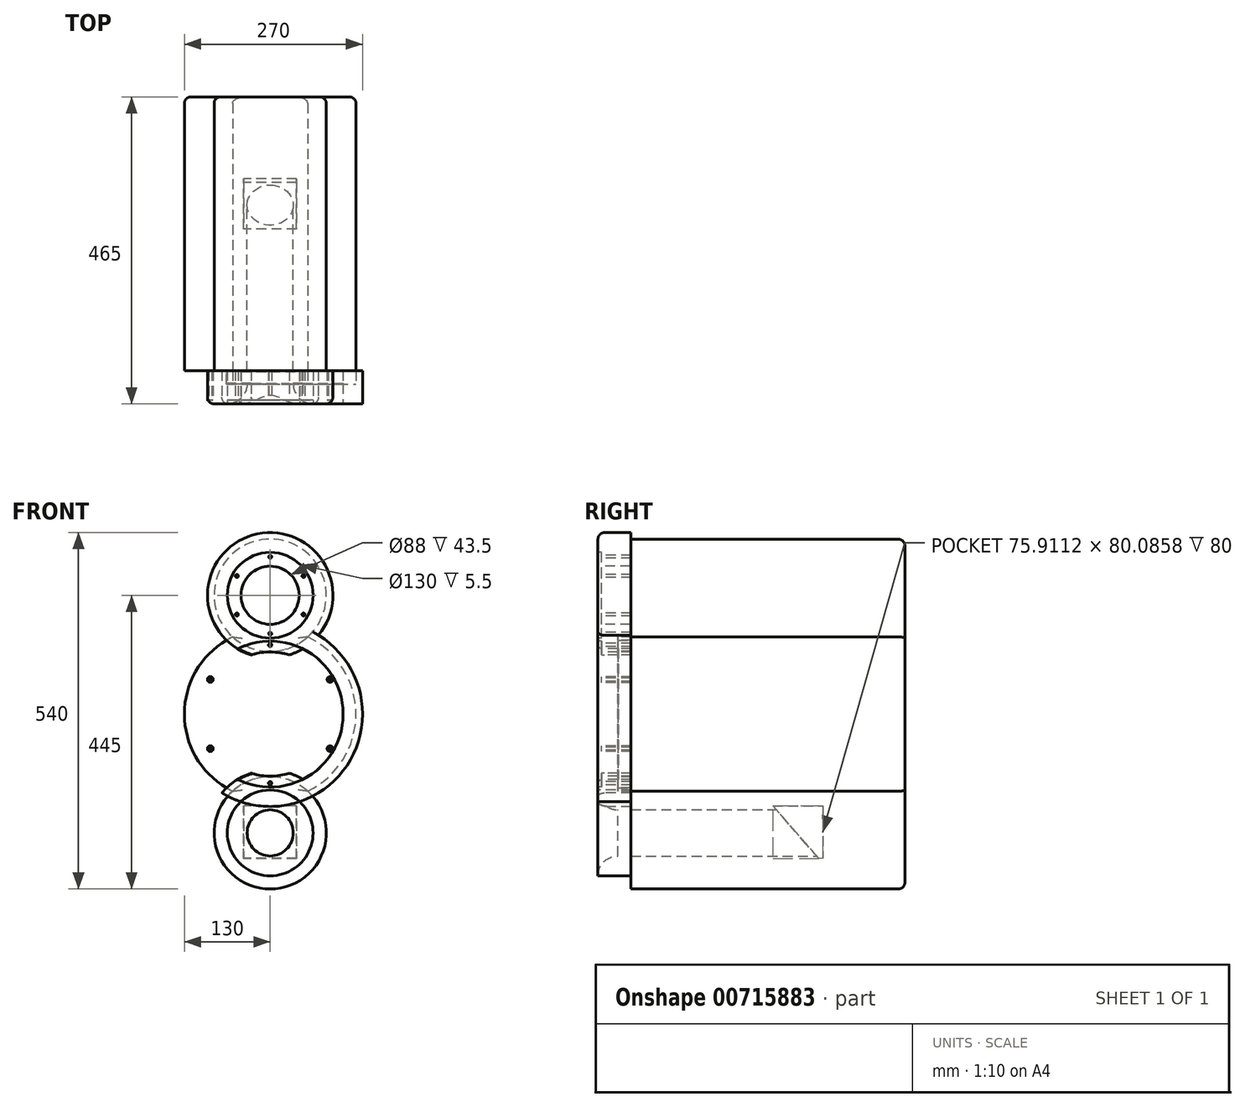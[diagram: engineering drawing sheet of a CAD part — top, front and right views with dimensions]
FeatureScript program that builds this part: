
annotation { "Feature Type Name" : "Feature", "Feature Type Description" : "" }
export const myFeature = defineFeature(function(context is Context, id is Id, definition is map)
    precondition{}
    {
        {
            var Q0;
            Q0=qCreatedBy(makeId("Front.planeOp"),FACE);
            var sketch = newSketch(context, id + "F0", { "sketchPlane" : qUnion([Q0])});
            skCircle(sketch, "E0", {"center": v(0, 0) * mm, "radius": 94 * mm});
            skCircle(sketch, "E1", {"center": v(0, 0) * mm, "radius": 110.5 * mm});
            skCircle(sketch, "E2", {"center": v(0, 180) * mm, "radius": 65 * mm});
            skCircle(sketch, "E3", {"center": v(0, 180) * mm, "radius": 44 * mm});
            skCircle(sketch, "E4", {"center": v(0, 104.75) * mm, "radius": 2.5 * mm});
            skCircle(sketch, "E5", {"center": v(0, 104.75) * mm, "radius": 4.4 * mm});
            skCircle(sketch, "E6.1.0", {"center": v(-90.72, 52.38) * mm, "radius": 4.4 * mm});
            skCircle(sketch, "E6.1.1", {"center": v(-90.72, 52.38) * mm, "radius": 2.5 * mm});
            skCircle(sketch, "E6.2.0", {"center": v(-90.72, -52.37) * mm, "radius": 4.4 * mm});
            skCircle(sketch, "E6.2.1", {"center": v(-90.72, -52.37) * mm, "radius": 2.5 * mm});
            skCircle(sketch, "E6.3.0", {"center": v(0, -104.75) * mm, "radius": 4.4 * mm});
            skCircle(sketch, "E6.3.1", {"center": v(0, -104.75) * mm, "radius": 2.5 * mm});
            skCircle(sketch, "E6.4.0", {"center": v(90.72, -52.38) * mm, "radius": 4.4 * mm});
            skCircle(sketch, "E6.4.1", {"center": v(90.72, -52.38) * mm, "radius": 2.5 * mm});
            skCircle(sketch, "E6.5.0", {"center": v(90.72, 52.38) * mm, "radius": 4.4 * mm});
            skCircle(sketch, "E6.5.1", {"center": v(90.72, 52.38) * mm, "radius": 2.5 * mm});
            skCircle(sketch, "E7", {"center": v(0, 238.25) * mm, "radius": 2.25 * mm});
            skCircle(sketch, "E8", {"center": v(0, 238.25) * mm, "radius": 4.25 * mm});
            skCircle(sketch, "E9.1.0", {"center": v(-50.45, 209.12) * mm, "radius": 4.25 * mm});
            skCircle(sketch, "E9.1.1", {"center": v(-50.45, 209.12) * mm, "radius": 2.25 * mm});
            skCircle(sketch, "E9.2.0", {"center": v(-50.45, 150.88) * mm, "radius": 4.25 * mm});
            skCircle(sketch, "E9.2.1", {"center": v(-50.45, 150.88) * mm, "radius": 2.25 * mm});
            skCircle(sketch, "E9.3.0", {"center": v(0, 121.75) * mm, "radius": 4.25 * mm});
            skCircle(sketch, "E9.3.1", {"center": v(0, 121.75) * mm, "radius": 2.25 * mm});
            skCircle(sketch, "E9.4.0", {"center": v(50.45, 150.87) * mm, "radius": 4.25 * mm});
            skCircle(sketch, "E9.4.1", {"center": v(50.45, 150.87) * mm, "radius": 2.25 * mm});
            skCircle(sketch, "E9.5.0", {"center": v(50.45, 209.12) * mm, "radius": 4.25 * mm});
            skCircle(sketch, "E9.5.1", {"center": v(50.45, 209.12) * mm, "radius": 2.25 * mm});
            skCircle(sketch, "E10", {"center": v(0, 180) * mm, "radius": 95 * mm});
            skCircle(sketch, "E11", {"center": v(0, 0) * mm, "radius": 140 * mm});
            skCircle(sketch, "E12", {"center": v(0, -180) * mm, "radius": 35 * mm});
            skCircle(sketch, "E13", {"center": v(0, -180) * mm, "radius": 95 * mm});
            skCircle(sketch, "E14", {"center": v(0, -180) * mm, "radius": 65 * mm});
            skSolve(sketch);
        }
        {
            var Q0;
            {var subQ0=sQuery(id+"F0.wireOp",EDGE,"E13");var subQ1=sQuery(id+"F0.wireOp",EDGE,"E11");var subQ2=makeQuery(id+"F0.imprint","INTERSECT",VERTEX,{"disambiguationData":[OD(0.0)],"derivedFrom":[subQ1,subQ0]});Q0=makeQuery(id+"F0.imprint","IMPRINT",FACE,{"disambiguationData":[TD([[makeQuery(id+"F0.imprint","IMPRINT",EDGE,{"disambiguationData":[TD([[subQ2,-1.0]])],"derivedFrom":subQ1}),-1.0]])]});}
            var Q1;
            Q1=makeQuery(id+"F0.imprint","IMPRINT",FACE,{"disambiguationData":[TD([[makeQuery(id+"F0.imprint","IMPRINT",EDGE,{"derivedFrom":sQuery(id+"F0.wireOp",EDGE,"E12")}),-1.0]])]});
            var Q2;
            Q2=makeQuery(id+"F0.imprint","IMPRINT",FACE,{"disambiguationData":[TD([[makeQuery(id+"F0.imprint","IMPRINT",EDGE,{"derivedFrom":sQuery(id+"F0.wireOp",EDGE,"E6.3.0")}),-1.0]])]});
            var Q3;
            {var subQ6=sQuery(id+"F0.wireOp",EDGE,"E10");var subQ8=sQuery(id+"F0.wireOp",EDGE,"E0");var subQ9=makeQuery(id+"F0.imprint","INTERSECT",VERTEX,{"disambiguationData":[OD(1.0)],"derivedFrom":[subQ8,subQ6]});Q3=makeQuery(id+"F0.imprint","IMPRINT",FACE,{"disambiguationData":[TD([[makeQuery(id+"F0.imprint","IMPRINT",EDGE,{"disambiguationData":[TD([[subQ9,1.0]])],"derivedFrom":subQ8}),-1.0]])]});}
            var Q4;
            {var subQ0=sQuery(id+"F0.wireOp",EDGE,"E10");var subQ1=sQuery(id+"F0.wireOp",EDGE,"E1");var subQ2=makeQuery(id+"F0.imprint","INTERSECT",VERTEX,{"disambiguationData":[OD(1.0)],"derivedFrom":[subQ1,subQ0]});Q4=makeQuery(id+"F0.imprint","IMPRINT",FACE,{"disambiguationData":[TD([[makeQuery(id+"F0.imprint","IMPRINT",EDGE,{"disambiguationData":[TD([[subQ2,1.0]])],"derivedFrom":subQ1}),-1.0]])]});}
            var Q5;
            {var subQ0=sQuery(id+"F0.wireOp",EDGE,"E10");var subQ1=sQuery(id+"F0.wireOp",EDGE,"E1");var subQ2=makeQuery(id+"F0.imprint","INTERSECT",VERTEX,{"disambiguationData":[OD(0.0)],"derivedFrom":[subQ1,subQ0]});Q5=makeQuery(id+"F0.imprint","IMPRINT",FACE,{"disambiguationData":[TD([[makeQuery(id+"F0.imprint","IMPRINT",EDGE,{"disambiguationData":[TD([[subQ2,-1.0]])],"derivedFrom":subQ1}),-1.0]])]});}
            var Q6;
            {var subQ4=sQuery(id+"F0.wireOp",EDGE,"E0");var subQ6=sQuery(id+"F0.wireOp",EDGE,"E10");var subQ10=makeQuery(id+"F0.imprint","INTERSECT",VERTEX,{"disambiguationData":[OD(0.0)],"derivedFrom":[subQ4,subQ6]});Q6=makeQuery(id+"F0.imprint","IMPRINT",FACE,{"disambiguationData":[TD([[makeQuery(id+"F0.imprint","IMPRINT",EDGE,{"disambiguationData":[TD([[subQ10,-1.0]])],"derivedFrom":subQ4}),-1.0]])]});}
            var Q7;
            {var subQ1=sQuery(id+"F0.wireOp",EDGE,"E10");var subQ3=sQuery(id+"F0.wireOp",EDGE,"E1");var subQ4=makeQuery(id+"F0.imprint","INTERSECT",VERTEX,{"disambiguationData":[OD(0.0)],"derivedFrom":[subQ3,subQ1]});Q7=makeQuery(id+"F0.imprint","IMPRINT",FACE,{"disambiguationData":[TD([[makeQuery(id+"F0.imprint","IMPRINT",EDGE,{"disambiguationData":[TD([[subQ4,1.0]])],"derivedFrom":subQ3}),-1.0]])]});}
            var Q8;
            Q8=makeQuery(id+"F0.imprint","IMPRINT",FACE,{"disambiguationData":[TD([[makeQuery(id+"F0.imprint","IMPRINT",EDGE,{"derivedFrom":sQuery(id+"F0.wireOp",EDGE,"E5")}),-1.0]])]});
            var Q9;
            Q9=makeQuery(id+"F0.imprint","IMPRINT",FACE,{"disambiguationData":[TD([[makeQuery(id+"F0.imprint","IMPRINT",EDGE,{"derivedFrom":sQuery(id+"F0.wireOp",EDGE,"E9.2.0")}),-1.0]])]});
            var Q10;
            Q10=makeQuery(id+"F0.imprint","IMPRINT",FACE,{"disambiguationData":[TD([[makeQuery(id+"F0.imprint","IMPRINT",EDGE,{"derivedFrom":sQuery(id+"F0.wireOp",EDGE,"E8")}),-1.0]])]});
            var Q11;
            {var subQ0=sQuery(id+"F0.wireOp",EDGE,"E11");var subQ1=sQuery(id+"F0.wireOp",EDGE,"E2");var subQ2=makeQuery(id+"F0.imprint","INTERSECT",VERTEX,{"disambiguationData":[OD(0.0)],"derivedFrom":[subQ1,subQ0]});Q11=makeQuery(id+"F0.imprint","IMPRINT",FACE,{"disambiguationData":[TD([[makeQuery(id+"F0.imprint","IMPRINT",EDGE,{"disambiguationData":[TD([[subQ2,-1.0]])],"derivedFrom":subQ1}),-1.0]])]});}
            var Q12;
            Q12=makeQuery(id+"F0.imprint","IMPRINT",FACE,{"disambiguationData":[TD([[makeQuery(id+"F0.imprint","IMPRINT",EDGE,{"derivedFrom":sQuery(id+"F0.wireOp",EDGE,"E6.3.0")}),1.0]])]});
            var Q13;
            {var subQ0=sQuery(id+"F0.wireOp",EDGE,"E13");var subQ1=sQuery(id+"F0.wireOp",EDGE,"E6.2.0");var subQ2=makeQuery(id+"F0.imprint","INTERSECT",VERTEX,{"disambiguationData":[OD(0.0)],"derivedFrom":[subQ1,subQ0]});Q13=makeQuery(id+"F0.imprint","IMPRINT",FACE,{"disambiguationData":[TD([[makeQuery(id+"F0.imprint","IMPRINT",EDGE,{"disambiguationData":[TD([[subQ2,1.0]])],"derivedFrom":subQ1}),1.0]])]});}
            var Q14;
            {var subQ0=sQuery(id+"F0.wireOp",EDGE,"E13");var subQ1=sQuery(id+"F0.wireOp",EDGE,"E6.2.0");var subQ2=makeQuery(id+"F0.imprint","INTERSECT",VERTEX,{"disambiguationData":[OD(0.0)],"derivedFrom":[subQ1,subQ0]});Q14=makeQuery(id+"F0.imprint","IMPRINT",FACE,{"disambiguationData":[TD([[makeQuery(id+"F0.imprint","IMPRINT",EDGE,{"disambiguationData":[TD([[subQ2,-1.0]])],"derivedFrom":subQ1}),1.0]])]});}
            var Q15;
            Q15=makeQuery(id+"F0.imprint","IMPRINT",FACE,{"disambiguationData":[TD([[makeQuery(id+"F0.imprint","IMPRINT",EDGE,{"derivedFrom":sQuery(id+"F0.wireOp",EDGE,"E6.1.0")}),1.0]])]});
            var Q16;
            Q16=makeQuery(id+"F0.imprint","IMPRINT",FACE,{"disambiguationData":[TD([[makeQuery(id+"F0.imprint","IMPRINT",EDGE,{"derivedFrom":sQuery(id+"F0.wireOp",EDGE,"E4")}),-1.0]])]});
            var Q17;
            Q17=makeQuery(id+"F0.imprint","IMPRINT",FACE,{"disambiguationData":[TD([[makeQuery(id+"F0.imprint","IMPRINT",EDGE,{"derivedFrom":sQuery(id+"F0.wireOp",EDGE,"E9.3.0")}),1.0]])]});
            var Q18;
            Q18=makeQuery(id+"F0.imprint","IMPRINT",FACE,{"disambiguationData":[TD([[makeQuery(id+"F0.imprint","IMPRINT",EDGE,{"derivedFrom":sQuery(id+"F0.wireOp",EDGE,"E6.5.0")}),1.0]])]});
            var Q19;
            {var subQ0=sQuery(id+"F0.wireOp",EDGE,"E13");var subQ1=sQuery(id+"F0.wireOp",EDGE,"E6.4.0");var subQ2=makeQuery(id+"F0.imprint","INTERSECT",VERTEX,{"disambiguationData":[OD(0.0)],"derivedFrom":[subQ1,subQ0]});Q19=makeQuery(id+"F0.imprint","IMPRINT",FACE,{"disambiguationData":[TD([[makeQuery(id+"F0.imprint","IMPRINT",EDGE,{"disambiguationData":[TD([[subQ2,-1.0]])],"derivedFrom":subQ1}),1.0]])]});}
            var Q20;
            {var subQ0=sQuery(id+"F0.wireOp",EDGE,"E13");var subQ1=sQuery(id+"F0.wireOp",EDGE,"E6.4.0");var subQ2=makeQuery(id+"F0.imprint","INTERSECT",VERTEX,{"disambiguationData":[OD(0.0)],"derivedFrom":[subQ1,subQ0]});Q20=makeQuery(id+"F0.imprint","IMPRINT",FACE,{"disambiguationData":[TD([[makeQuery(id+"F0.imprint","IMPRINT",EDGE,{"disambiguationData":[TD([[subQ2,1.0]])],"derivedFrom":subQ1}),1.0]])]});}
            var Q21;
            Q21=makeQuery(id+"F0.imprint","IMPRINT",FACE,{"disambiguationData":[TD([[makeQuery(id+"F0.imprint","IMPRINT",EDGE,{"derivedFrom":sQuery(id+"F0.wireOp",EDGE,"E9.4.0")}),1.0]])]});
            var Q22;
            Q22=makeQuery(id+"F0.imprint","IMPRINT",FACE,{"disambiguationData":[TD([[makeQuery(id+"F0.imprint","IMPRINT",EDGE,{"derivedFrom":sQuery(id+"F0.wireOp",EDGE,"E9.2.0")}),1.0]])]});
            var Q23;
            Q23=makeQuery(id+"F0.imprint","IMPRINT",FACE,{"disambiguationData":[TD([[makeQuery(id+"F0.imprint","IMPRINT",EDGE,{"derivedFrom":sQuery(id+"F0.wireOp",EDGE,"E9.1.0")}),1.0]])]});
            var Q24;
            Q24=makeQuery(id+"F0.imprint","IMPRINT",FACE,{"disambiguationData":[TD([[makeQuery(id+"F0.imprint","IMPRINT",EDGE,{"derivedFrom":sQuery(id+"F0.wireOp",EDGE,"E7")}),-1.0]])]});
            var Q25;
            Q25=makeQuery(id+"F0.imprint","IMPRINT",FACE,{"disambiguationData":[TD([[makeQuery(id+"F0.imprint","IMPRINT",EDGE,{"derivedFrom":sQuery(id+"F0.wireOp",EDGE,"E9.5.0")}),1.0]])]});
            var Q26;
            {var subQ0=sQuery(id+"F0.wireOp",EDGE,"E13");var subQ7=sQuery(id+"F0.wireOp",EDGE,"E1");var subQ9=makeQuery(id+"F0.imprint","INTERSECT",VERTEX,{"disambiguationData":[OD(0.0)],"derivedFrom":[subQ7,subQ0]});Q26=makeQuery(id+"F0.imprint","IMPRINT",FACE,{"disambiguationData":[TD([[makeQuery(id+"F0.imprint","IMPRINT",EDGE,{"disambiguationData":[TD([[subQ9,-1.0]])],"derivedFrom":subQ7}),-1.0]])]});}
            var Q27;
            Q27=makeQuery(id+"F0.imprint","IMPRINT",FACE,{"disambiguationData":[TD([[makeQuery(id+"F0.imprint","IMPRINT",EDGE,{"derivedFrom":sQuery(id+"F0.wireOp",EDGE,"E6.4.0")}),1.0]])]});
            var Q28;
            Q28=makeQuery(id+"F0.imprint","IMPRINT",FACE,{"disambiguationData":[TD([[makeQuery(id+"F0.imprint","IMPRINT",EDGE,{"derivedFrom":sQuery(id+"F0.wireOp",EDGE,"E6.2.0")}),1.0]])]});
            var Q29;
            Q29=makeQuery(id+"F0.imprint","IMPRINT",FACE,{"disambiguationData":[TD([[makeQuery(id+"F0.imprint","IMPRINT",EDGE,{"derivedFrom":sQuery(id+"F0.wireOp",EDGE,"E9.3.0")}),-1.0]])]});
            var Q30;
            {var subQ0=sQuery(id+"F0.wireOp",EDGE,"E14");var subQ1=sQuery(id+"F0.wireOp",EDGE,"E11");var subQ2=makeQuery(id+"F0.imprint","INTERSECT",VERTEX,{"disambiguationData":[OD(0.0)],"derivedFrom":[subQ1,subQ0]});Q30=makeQuery(id+"F0.imprint","IMPRINT",FACE,{"disambiguationData":[TD([[makeQuery(id+"F0.imprint","IMPRINT",EDGE,{"disambiguationData":[TD([[subQ2,-1.0]])],"derivedFrom":subQ1}),1.0]])]});}
            extrude(context, id + "F1", {"entities" : qUnion([Q0, Q1, Q2, Q3, Q4, Q5, Q6, Q7, Q8, Q9, Q10, Q11, Q12, Q13, Q14, Q15, Q16, Q17, Q18, Q19, Q20, Q21, Q22, Q23, Q24, Q25, Q26, Q27, Q28, Q29, Q30]), "depth" : -50 * mm, "offsetDistance" : 25 * mm});
        }
        {
            var Q0;
            Q0=makeQuery(id+"F0.imprint","IMPRINT",FACE,{"disambiguationData":[TD([[makeQuery(id+"F0.imprint","IMPRINT",EDGE,{"derivedFrom":sQuery(id+"F0.wireOp",EDGE,"E6.3.0")}),-1.0]])]});
            var Q1;
            Q1=makeQuery(id+"F0.imprint","IMPRINT",FACE,{"disambiguationData":[TD([[makeQuery(id+"F0.imprint","IMPRINT",EDGE,{"derivedFrom":sQuery(id+"F0.wireOp",EDGE,"E6.3.0")}),1.0]])]});
            var Q2;
            {var subQ0=sQuery(id+"F0.wireOp",EDGE,"E13");var subQ1=sQuery(id+"F0.wireOp",EDGE,"E6.2.0");var subQ2=makeQuery(id+"F0.imprint","INTERSECT",VERTEX,{"disambiguationData":[OD(0.0)],"derivedFrom":[subQ1,subQ0]});Q2=makeQuery(id+"F0.imprint","IMPRINT",FACE,{"disambiguationData":[TD([[makeQuery(id+"F0.imprint","IMPRINT",EDGE,{"disambiguationData":[TD([[subQ2,1.0]])],"derivedFrom":subQ1}),1.0]])]});}
            var Q3;
            {var subQ0=sQuery(id+"F0.wireOp",EDGE,"E13");var subQ1=sQuery(id+"F0.wireOp",EDGE,"E6.2.0");var subQ2=makeQuery(id+"F0.imprint","INTERSECT",VERTEX,{"disambiguationData":[OD(0.0)],"derivedFrom":[subQ1,subQ0]});Q3=makeQuery(id+"F0.imprint","IMPRINT",FACE,{"disambiguationData":[TD([[makeQuery(id+"F0.imprint","IMPRINT",EDGE,{"disambiguationData":[TD([[subQ2,-1.0]])],"derivedFrom":subQ1}),1.0]])]});}
            var Q4;
            {var subQ4=sQuery(id+"F0.wireOp",EDGE,"E0");var subQ6=sQuery(id+"F0.wireOp",EDGE,"E10");var subQ10=makeQuery(id+"F0.imprint","INTERSECT",VERTEX,{"disambiguationData":[OD(0.0)],"derivedFrom":[subQ4,subQ6]});Q4=makeQuery(id+"F0.imprint","IMPRINT",FACE,{"disambiguationData":[TD([[makeQuery(id+"F0.imprint","IMPRINT",EDGE,{"disambiguationData":[TD([[subQ10,-1.0]])],"derivedFrom":subQ4}),-1.0]])]});}
            var Q5;
            Q5=makeQuery(id+"F0.imprint","IMPRINT",FACE,{"disambiguationData":[TD([[makeQuery(id+"F0.imprint","IMPRINT",EDGE,{"derivedFrom":sQuery(id+"F0.wireOp",EDGE,"E5")}),-1.0]])]});
            var Q6;
            Q6=makeQuery(id+"F0.imprint","IMPRINT",FACE,{"disambiguationData":[TD([[makeQuery(id+"F0.imprint","IMPRINT",EDGE,{"derivedFrom":sQuery(id+"F0.wireOp",EDGE,"E6.1.0")}),1.0]])]});
            var Q7;
            Q7=makeQuery(id+"F0.imprint","IMPRINT",FACE,{"disambiguationData":[TD([[makeQuery(id+"F0.imprint","IMPRINT",EDGE,{"derivedFrom":sQuery(id+"F0.wireOp",EDGE,"E4")}),-1.0]])]});
            var Q8;
            Q8=makeQuery(id+"F0.imprint","IMPRINT",FACE,{"disambiguationData":[TD([[makeQuery(id+"F0.imprint","IMPRINT",EDGE,{"derivedFrom":sQuery(id+"F0.wireOp",EDGE,"E6.5.0")}),1.0]])]});
            var Q9;
            {var subQ6=sQuery(id+"F0.wireOp",EDGE,"E10");var subQ8=sQuery(id+"F0.wireOp",EDGE,"E0");var subQ9=makeQuery(id+"F0.imprint","INTERSECT",VERTEX,{"disambiguationData":[OD(1.0)],"derivedFrom":[subQ8,subQ6]});Q9=makeQuery(id+"F0.imprint","IMPRINT",FACE,{"disambiguationData":[TD([[makeQuery(id+"F0.imprint","IMPRINT",EDGE,{"disambiguationData":[TD([[subQ9,1.0]])],"derivedFrom":subQ8}),-1.0]])]});}
            var Q10;
            {var subQ0=sQuery(id+"F0.wireOp",EDGE,"E13");var subQ1=sQuery(id+"F0.wireOp",EDGE,"E6.4.0");var subQ2=makeQuery(id+"F0.imprint","INTERSECT",VERTEX,{"disambiguationData":[OD(0.0)],"derivedFrom":[subQ1,subQ0]});Q10=makeQuery(id+"F0.imprint","IMPRINT",FACE,{"disambiguationData":[TD([[makeQuery(id+"F0.imprint","IMPRINT",EDGE,{"disambiguationData":[TD([[subQ2,-1.0]])],"derivedFrom":subQ1}),1.0]])]});}
            var Q11;
            {var subQ0=sQuery(id+"F0.wireOp",EDGE,"E13");var subQ1=sQuery(id+"F0.wireOp",EDGE,"E6.4.0");var subQ2=makeQuery(id+"F0.imprint","INTERSECT",VERTEX,{"disambiguationData":[OD(0.0)],"derivedFrom":[subQ1,subQ0]});Q11=makeQuery(id+"F0.imprint","IMPRINT",FACE,{"disambiguationData":[TD([[makeQuery(id+"F0.imprint","IMPRINT",EDGE,{"disambiguationData":[TD([[subQ2,1.0]])],"derivedFrom":subQ1}),1.0]])]});}
            var Q12;
            Q12=makeQuery(id+"F0.imprint","IMPRINT",FACE,{"disambiguationData":[TD([[makeQuery(id+"F0.imprint","IMPRINT",EDGE,{"derivedFrom":sQuery(id+"F0.wireOp",EDGE,"E9.2.0")}),-1.0]])]});
            var Q13;
            Q13=makeQuery(id+"F0.imprint","IMPRINT",FACE,{"disambiguationData":[TD([[makeQuery(id+"F0.imprint","IMPRINT",EDGE,{"derivedFrom":sQuery(id+"F0.wireOp",EDGE,"E9.4.0")}),1.0]])]});
            var Q14;
            Q14=makeQuery(id+"F0.imprint","IMPRINT",FACE,{"disambiguationData":[TD([[makeQuery(id+"F0.imprint","IMPRINT",EDGE,{"derivedFrom":sQuery(id+"F0.wireOp",EDGE,"E9.2.0")}),1.0]])]});
            var Q15;
            Q15=makeQuery(id+"F0.imprint","IMPRINT",FACE,{"disambiguationData":[TD([[makeQuery(id+"F0.imprint","IMPRINT",EDGE,{"derivedFrom":sQuery(id+"F0.wireOp",EDGE,"E9.1.0")}),1.0]])]});
            var Q16;
            Q16=makeQuery(id+"F0.imprint","IMPRINT",FACE,{"disambiguationData":[TD([[makeQuery(id+"F0.imprint","IMPRINT",EDGE,{"derivedFrom":sQuery(id+"F0.wireOp",EDGE,"E8")}),-1.0]])]});
            var Q17;
            Q17=makeQuery(id+"F0.imprint","IMPRINT",FACE,{"disambiguationData":[TD([[makeQuery(id+"F0.imprint","IMPRINT",EDGE,{"derivedFrom":sQuery(id+"F0.wireOp",EDGE,"E7")}),-1.0]])]});
            var Q18;
            Q18=makeQuery(id+"F0.imprint","IMPRINT",FACE,{"disambiguationData":[TD([[makeQuery(id+"F0.imprint","IMPRINT",EDGE,{"derivedFrom":sQuery(id+"F0.wireOp",EDGE,"E9.5.0")}),1.0]])]});
            var Q19;
            Q19=makeQuery(id+"F0.imprint","IMPRINT",FACE,{"disambiguationData":[TD([[makeQuery(id+"F0.imprint","IMPRINT",EDGE,{"derivedFrom":sQuery(id+"F0.wireOp",EDGE,"E6.2.0")}),1.0]])]});
            var Q20;
            Q20=makeQuery(id+"F0.imprint","IMPRINT",FACE,{"disambiguationData":[TD([[makeQuery(id+"F0.imprint","IMPRINT",EDGE,{"derivedFrom":sQuery(id+"F0.wireOp",EDGE,"E6.4.0")}),1.0]])]});
            var Q21;
            Q21=makeQuery(id+"F0.imprint","IMPRINT",FACE,{"disambiguationData":[TD([[makeQuery(id+"F0.imprint","IMPRINT",EDGE,{"derivedFrom":sQuery(id+"F0.wireOp",EDGE,"E9.3.0")}),-1.0]])]});
            var Q22;
            Q22=makeQuery(id+"F0.imprint","IMPRINT",FACE,{"disambiguationData":[TD([[makeQuery(id+"F0.imprint","IMPRINT",EDGE,{"derivedFrom":sQuery(id+"F0.wireOp",EDGE,"E9.3.0")}),1.0]])]});
            extrude(context, id + "F2", {"entities" : qUnion([Q0, Q1, Q2, Q3, Q4, Q5, Q6, Q7, Q8, Q9, Q10, Q11, Q12, Q13, Q14, Q15, Q16, Q17, Q18, Q19, Q20, Q21, Q22]), "operationType" : NewBodyOperationType.REMOVE, "oppositeDirection" : true, "depth" : 5.5 * mm, "offsetDistance" : 25 * mm});
        }
        {
            var Q0;
            Q0=makeQuery(id+"F1.opExtrude","CAP_EDGE",EDGE,{"disambiguationData":[OSD([sQuery(id+"F0.wireOp",EDGE,"E12")])],"isStart":true});
            fillet(context, id + "F3", {"entities" : qUnion([Q0]), "radius" : 30 * mm, "tangentPropagation" : true, "allowEdgeOverflow" : false});
        }
        {
            var Q0;
            Q0=makeQuery(id+"F1.opExtrude","CAP_FACE",FACE,{"disambiguationData":[OSD([sQuery(id+"F0.wireOp",EDGE,"E0"),sQuery(id+"F0.wireOp",EDGE,"E3"),sQuery(id+"F0.wireOp",EDGE,"E4"),sQuery(id+"F0.wireOp",EDGE,"E6.1.1"),sQuery(id+"F0.wireOp",EDGE,"E6.2.1"),sQuery(id+"F0.wireOp",EDGE,"E6.3.1"),sQuery(id+"F0.wireOp",EDGE,"E6.4.1"),sQuery(id+"F0.wireOp",EDGE,"E6.5.1"),sQuery(id+"F0.wireOp",EDGE,"E7"),sQuery(id+"F0.wireOp",EDGE,"E9.1.1"),sQuery(id+"F0.wireOp",EDGE,"E9.2.1"),sQuery(id+"F0.wireOp",EDGE,"E9.3.1"),sQuery(id+"F0.wireOp",EDGE,"E9.4.1"),sQuery(id+"F0.wireOp",EDGE,"E9.5.1"),sQuery(id+"F0.wireOp",EDGE,"E10"),sQuery(id+"F0.wireOp",EDGE,"E11"),sQuery(id+"F0.wireOp",EDGE,"E12"),sQuery(id+"F0.wireOp",EDGE,"E13")])],"isStart":false});
            var sketch = newSketch(context, id + "F4", { "sketchPlane" : qUnion([Q0])});
            skCircle(sketch, "E15", {"center": v(0, -180) * mm, "radius": 35 * mm});
            skCircle(sketch, "E16", {"center": v(0, -180) * mm, "radius": 39 * mm});
            skSolve(sketch);
        }
        {
            var Q0;
            Q0=makeQuery(id+"F4.imprint","IMPRINT",FACE,{"disambiguationData":[TD([[makeQuery(id+"F4.imprint","IMPRINT",EDGE,{"derivedFrom":sQuery(id+"F4.wireOp",EDGE,"E15")}),1.0]])]});
            extrude(context, id + "F5", {"entities" : qUnion([Q0]), "operationType" : NewBodyOperationType.REMOVE, "oppositeDirection" : true, "depth" : 20 * mm, "offsetDistance" : 25 * mm});
        }
        {
            var Q0;
            Q0=makeQuery(id+"F4.imprint","IMPRINT",FACE,{"disambiguationData":[TD([[makeQuery(id+"F4.imprint","IMPRINT",EDGE,{"derivedFrom":sQuery(id+"F4.wireOp",EDGE,"E15")}),1.0]])]});
            extrude(context, id + "F6", {"entities" : qUnion([Q0]), "depth" : -20 * mm, "offsetDistance" : 25 * mm});
        }
        {
            var Q0;
            Q0=makeQuery(id+"F4.imprint","IMPRINT",FACE,{"disambiguationData":[TD([[makeQuery(id+"F4.imprint","IMPRINT",EDGE,{"derivedFrom":sQuery(id+"F4.wireOp",EDGE,"E15")}),1.0]])]});
            extrude(context, id + "F7", {"entities" : qUnion([Q0]), "operationType" : NewBodyOperationType.ADD, "depth" : 285 * mm, "offsetDistance" : 25 * mm});
        }
        {
            var Q0;
            Q0=makeQuery(id+"F1.opExtrude","CAP_FACE",FACE,{"disambiguationData":[OSD([sQuery(id+"F0.wireOp",EDGE,"E0"),sQuery(id+"F0.wireOp",EDGE,"E3"),sQuery(id+"F0.wireOp",EDGE,"E4"),sQuery(id+"F0.wireOp",EDGE,"E6.1.1"),sQuery(id+"F0.wireOp",EDGE,"E6.2.1"),sQuery(id+"F0.wireOp",EDGE,"E6.3.1"),sQuery(id+"F0.wireOp",EDGE,"E6.4.1"),sQuery(id+"F0.wireOp",EDGE,"E6.5.1"),sQuery(id+"F0.wireOp",EDGE,"E7"),sQuery(id+"F0.wireOp",EDGE,"E9.1.1"),sQuery(id+"F0.wireOp",EDGE,"E9.2.1"),sQuery(id+"F0.wireOp",EDGE,"E9.3.1"),sQuery(id+"F0.wireOp",EDGE,"E9.4.1"),sQuery(id+"F0.wireOp",EDGE,"E9.5.1"),sQuery(id+"F0.wireOp",EDGE,"E10"),sQuery(id+"F0.wireOp",EDGE,"E11"),sQuery(id+"F0.wireOp",EDGE,"E12"),sQuery(id+"F0.wireOp",EDGE,"E13")])],"isStart":false});
            var sketch = newSketch(context, id + "F8", { "sketchPlane" : qUnion([Q0])});
            skCircle(sketch, "E17", {"center": v(0, 0) * mm, "radius": 130 * mm});
            skCircle(sketch, "E18", {"center": v(0, 180) * mm, "radius": 85 * mm});
            skCircle(sketch, "E19", {"center": v(0, -180) * mm, "radius": 85 * mm});
            skSolve(sketch);
        }
        {
            var Q0;
            Q0 = qSketchRegion(id + "F8", true);
            extrude(context, id + "F9", {"entities" : qUnion([Q0]), "depth" : 365 * mm, "offsetDistance" : 25 * mm});
        }
        {
            var Q0;
            {var subQ9=sQuery(id+"F0.wireOp",EDGE,"E10");Q0=makeQuery(id+"F8.imprint","IMPRINT",FACE,{"disambiguationData":[TD([[makeQuery(id+"F8.imprint","IMPRINT",EDGE,{"derivedFrom":makeQuery(id+"F1.opExtrude","CAP_EDGE",EDGE,{"disambiguationData":[OSD([subQ9])],"isStart":false})}),-1.0]])]});}
            extrude(context, id + "F10", {"entities" : qUnion([Q0]), "operationType" : NewBodyOperationType.REMOVE, "oppositeDirection" : true, "depth" : 20 * mm, "offsetDistance" : 25 * mm});
        }
        {
            var Q0;
            Q0=makeQuery(id+"F10.boolean.opBoolean","COPY",FACE,{"derivedFrom":makeQuery(id+"F10.opExtrude","CAP_FACE",FACE,{"disambiguationData":[OSD([sQuery(id+"F0.wireOp",EDGE,"E10"),sQuery(id+"F0.wireOp",EDGE,"E11"),sQuery(id+"F0.wireOp",EDGE,"E13"),sQuery(id+"F8.wireOp",EDGE,"E17"),sQuery(id+"F8.wireOp",EDGE,"E18"),sQuery(id+"F8.wireOp",EDGE,"E19")])],"isStart":false})});
            extrude(context, id + "F11", {"entities" : qUnion([Q0]), "depth" : 385 * mm, "offsetDistance" : 25 * mm});
        }
        {
            var Q0;
            Q0=makeQuery(id+"F9.opExtrude","CAP_FACE",FACE,{"disambiguationData":[OSD([sQuery(id+"F8.wireOp",EDGE,"E17"),sQuery(id+"F8.wireOp",EDGE,"E18"),sQuery(id+"F8.wireOp",EDGE,"E19")])],"isStart":false});
            var Q1;
            Q1=makeQuery(id+"F11.opExtrude","CAP_FACE",FACE,{"disambiguationData":[OSD([sQuery(id+"F0.wireOp",EDGE,"E10"),sQuery(id+"F0.wireOp",EDGE,"E11"),sQuery(id+"F0.wireOp",EDGE,"E13"),sQuery(id+"F8.wireOp",EDGE,"E17"),sQuery(id+"F8.wireOp",EDGE,"E18"),sQuery(id+"F8.wireOp",EDGE,"E19")])],"isStart":false});
            extrude(context, id + "F12", {"entities" : qUnion([Q0, Q1]), "depth" : 50 * mm, "offsetDistance" : 25 * mm});
        }
        {
            var Q0;
            Q0=makeQuery(id+"F12.opExtrude","CAP_FACE",FACE,{"disambiguationData":[OSD([sQuery(id+"F0.wireOp",EDGE,"E10"),sQuery(id+"F0.wireOp",EDGE,"E11"),sQuery(id+"F0.wireOp",EDGE,"E13"),sQuery(id+"F8.wireOp",EDGE,"E17"),sQuery(id+"F8.wireOp",EDGE,"E18"),sQuery(id+"F8.wireOp",EDGE,"E19")])],"isStart":true});
            extrude(context, id + "F13", {"entities" : qUnion([Q0]), "operationType" : NewBodyOperationType.REMOVE, "oppositeDirection" : true, "depth" : 20 * mm, "offsetDistance" : 25 * mm});
        }
        {
            var Q0;
            Q0=makeQuery(id+"F12.opExtrude","SWEPT_BODY",BODY,{"disambiguationData":[OSD([sQuery(id+"F0.wireOp",EDGE,"E10"),sQuery(id+"F0.wireOp",EDGE,"E11"),sQuery(id+"F0.wireOp",EDGE,"E13"),sQuery(id+"F8.wireOp",EDGE,"E17"),sQuery(id+"F8.wireOp",EDGE,"E18"),sQuery(id+"F8.wireOp",EDGE,"E19")])]});
            var Q1;
            Q1=makeQuery(id+"F12.opExtrude","SWEPT_BODY",BODY,{"disambiguationData":[OSD([sQuery(id+"F8.wireOp",EDGE,"E17"),sQuery(id+"F8.wireOp",EDGE,"E18"),sQuery(id+"F8.wireOp",EDGE,"E19")])]});
            booleanBodies(context, id + "F14", {"operationType" : BooleanOperationType.UNION, "tools" : qUnion([Q0, Q1])});
        }
        {
            var Q0;
            Q0=makeQuery(id+"F11.opExtrude","CAP_FACE",FACE,{"disambiguationData":[OSD([sQuery(id+"F0.wireOp",EDGE,"E10"),sQuery(id+"F0.wireOp",EDGE,"E11"),sQuery(id+"F0.wireOp",EDGE,"E13"),sQuery(id+"F8.wireOp",EDGE,"E17"),sQuery(id+"F8.wireOp",EDGE,"E18"),sQuery(id+"F8.wireOp",EDGE,"E19")])],"isStart":false});
            extrude(context, id + "F15", {"entities" : qUnion([Q0]), "operationType" : NewBodyOperationType.ADD, "depth" : 20 * mm, "offsetDistance" : 25 * mm});
        }
        {
            var Q0;
            {var subQ0=sQuery(id+"F0.wireOp",EDGE,"E11");Q0=makeQuery(id+"F1.opExtrude","CAP_EDGE",EDGE,{"disambiguationData":[OSD([subQ0]),TDD([makeQuery(id+"F0.imprint","IMPRINT",EDGE,{"disambiguationData":[TD([[makeQuery(id+"F0.imprint","INTERSECT",VERTEX,{"disambiguationData":[OD(0.0)],"derivedFrom":[sQuery(id+"F0.wireOp",EDGE,"E10"),subQ0]}),-1.0]])],"derivedFrom":subQ0})])],"isStart":true});}
            var Q1;
            Q1=makeQuery(id+"F1.opExtrude","CAP_EDGE",EDGE,{"disambiguationData":[OSD([sQuery(id+"F0.wireOp",EDGE,"E10")])],"isStart":true});
            var Q2;
            {var subQ0=sQuery(id+"F0.wireOp",EDGE,"E11");Q2=makeQuery(id+"F1.opExtrude","CAP_EDGE",EDGE,{"disambiguationData":[OSD([subQ0]),TDD([makeQuery(id+"F0.imprint","IMPRINT",EDGE,{"disambiguationData":[TD([[makeQuery(id+"F0.imprint","INTERSECT",VERTEX,{"disambiguationData":[OD(1.0)],"derivedFrom":[sQuery(id+"F0.wireOp",EDGE,"E10"),subQ0]}),1.0]])],"derivedFrom":subQ0})])],"isStart":true});}
            var Q3;
            Q3=makeQuery(id+"F1.opExtrude","CAP_EDGE",EDGE,{"disambiguationData":[OSD([sQuery(id+"F0.wireOp",EDGE,"E13")])],"isStart":true});
            var Q4;
            Q4=makeQuery(id+"F12.opExtrude","CAP_EDGE",EDGE,{"disambiguationData":[OSD([sQuery(id+"F0.wireOp",EDGE,"E13")])],"isStart":false});
            var Q5;
            {var subQ0=sQuery(id+"F0.wireOp",EDGE,"E11");Q5=makeQuery(id+"F12.opExtrude","CAP_EDGE",EDGE,{"disambiguationData":[OSD([subQ0]),TDD([makeQuery(id+"F11.opExtrude","CAP_EDGE",EDGE,{"disambiguationData":[OSD([subQ0]),TDD([makeQuery(id+"F10.boolean.opBoolean","COPY",EDGE,{"derivedFrom":makeQuery(id+"F10.opExtrude","CAP_EDGE",EDGE,{"disambiguationData":[OSD([subQ0]),TDD([makeQuery(id+"F8.imprint","IMPRINT",EDGE,{"derivedFrom":makeQuery(id+"F1.opExtrude","CAP_EDGE",EDGE,{"disambiguationData":[OSD([subQ0]),TDD([makeQuery(id+"F0.imprint","IMPRINT",EDGE,{"disambiguationData":[TD([[makeQuery(id+"F0.imprint","INTERSECT",VERTEX,{"disambiguationData":[OD(0.0)],"derivedFrom":[sQuery(id+"F0.wireOp",EDGE,"E10"),subQ0]}),-1.0]])],"derivedFrom":subQ0})])],"isStart":false})})])],"isStart":false})})])],"isStart":false})])],"isStart":false});}
            var Q6;
            {var subQ0=sQuery(id+"F8.wireOp",EDGE,"E19");var subQ1=sQuery(id+"F8.wireOp",EDGE,"E18");var subQ2=sQuery(id+"F8.wireOp",EDGE,"E17");Q6=makeQuery(id+"F14.opBoolean","MERGE",FACE,{"derivedFrom":[makeQuery(id+"F12.opExtrude","CAP_FACE",FACE,{"disambiguationData":[OSD([subQ2,subQ1,subQ0])],"isStart":false}),makeQuery(id+"F12.opExtrude","CAP_FACE",FACE,{"disambiguationData":[OSD([sQuery(id+"F0.wireOp",EDGE,"E10"),sQuery(id+"F0.wireOp",EDGE,"E11"),sQuery(id+"F0.wireOp",EDGE,"E13"),subQ2,subQ1,subQ0])],"isStart":false})]});}
            fillet(context, id + "F16", {"entities" : qUnion([Q0, Q1, Q2, Q3, Q4, Q5, Q6]), "radius" : 10 * mm, "tangentPropagation" : true, "allowEdgeOverflow" : false});
        }
        {
            var Q0;
            Q0=makeQuery(id+"F10.boolean.opBoolean","COPY",EDGE,{"derivedFrom":makeQuery(id+"F10.opExtrude","CAP_EDGE",EDGE,{"disambiguationData":[OSD([sQuery(id+"F8.wireOp",EDGE,"E18")])],"isStart":true})});
            var Q1;
            {var subQ0=sQuery(id+"F8.wireOp",EDGE,"E17");Q1=makeQuery(id+"F10.boolean.opBoolean","COPY",EDGE,{"derivedFrom":makeQuery(id+"F10.opExtrude","CAP_EDGE",EDGE,{"disambiguationData":[OSD([subQ0]),TDD([makeQuery(id+"F8.imprint","IMPRINT",EDGE,{"disambiguationData":[TD([[makeQuery(id+"F8.imprint","INTERSECT",VERTEX,{"disambiguationData":[OD(1.0)],"derivedFrom":[subQ0,sQuery(id+"F8.wireOp",EDGE,"E18")]}),1.0]])],"derivedFrom":subQ0})])],"isStart":true})});}
            var Q2;
            Q2=makeQuery(id+"F10.boolean.opBoolean","COPY",EDGE,{"derivedFrom":makeQuery(id+"F10.opExtrude","CAP_EDGE",EDGE,{"disambiguationData":[OSD([sQuery(id+"F8.wireOp",EDGE,"E19")])],"isStart":true})});
            var Q3;
            {var subQ0=sQuery(id+"F8.wireOp",EDGE,"E17");Q3=makeQuery(id+"F10.boolean.opBoolean","COPY",EDGE,{"derivedFrom":makeQuery(id+"F10.opExtrude","CAP_EDGE",EDGE,{"disambiguationData":[OSD([subQ0]),TDD([makeQuery(id+"F8.imprint","IMPRINT",EDGE,{"disambiguationData":[TD([[makeQuery(id+"F8.imprint","INTERSECT",VERTEX,{"disambiguationData":[OD(0.0)],"derivedFrom":[subQ0,sQuery(id+"F8.wireOp",EDGE,"E18")]}),-1.0]])],"derivedFrom":subQ0})])],"isStart":true})});}
            var Q4;
            Q4=makeQuery(id+"F1.opExtrude","CAP_EDGE",EDGE,{"disambiguationData":[OSD([sQuery(id+"F0.wireOp",EDGE,"E3")])],"isStart":false});
            var Q5;
            Q5=makeQuery(id+"F1.opExtrude","CAP_EDGE",EDGE,{"disambiguationData":[OSD([sQuery(id+"F0.wireOp",EDGE,"E0")])],"isStart":false});
            var Q6;
            Q6=makeQuery(id+"F2.boolean.opBoolean","COPY",EDGE,{"derivedFrom":makeQuery(id+"F2.opExtrude","CAP_EDGE",EDGE,{"disambiguationData":[OSD([sQuery(id+"F0.wireOp",EDGE,"E3")])],"isStart":false})});
            var Q7;
            Q7=makeQuery(id+"F2.boolean.opBoolean","COPY",EDGE,{"derivedFrom":makeQuery(id+"F2.opExtrude","CAP_EDGE",EDGE,{"disambiguationData":[OSD([sQuery(id+"F0.wireOp",EDGE,"E0")])],"isStart":false})});
            var Q8;
            Q8=makeQuery(id+"F2.boolean.opBoolean","COPY",EDGE,{"derivedFrom":makeQuery(id+"F2.opExtrude","CAP_EDGE",EDGE,{"disambiguationData":[OSD([sQuery(id+"F0.wireOp",EDGE,"E2")])],"isStart":true})});
            var Q9;
            Q9=makeQuery(id+"F2.boolean.opBoolean","COPY",EDGE,{"derivedFrom":makeQuery(id+"F2.opExtrude","CAP_EDGE",EDGE,{"disambiguationData":[OSD([sQuery(id+"F0.wireOp",EDGE,"E1")])],"isStart":true})});
            var Q10;
            Q10=makeQuery(id+"F10.boolean.opBoolean","COPY",EDGE,{"derivedFrom":makeQuery(id+"F10.opExtrude","CAP_EDGE",EDGE,{"disambiguationData":[OSD([sQuery(id+"F0.wireOp",EDGE,"E10")])],"isStart":false})});
            var Q11;
            {var subQ0=sQuery(id+"F0.wireOp",EDGE,"E11");Q11=makeQuery(id+"F10.boolean.opBoolean","COPY",EDGE,{"derivedFrom":makeQuery(id+"F10.opExtrude","CAP_EDGE",EDGE,{"disambiguationData":[OSD([subQ0]),TDD([makeQuery(id+"F8.imprint","IMPRINT",EDGE,{"derivedFrom":makeQuery(id+"F1.opExtrude","CAP_EDGE",EDGE,{"disambiguationData":[OSD([subQ0]),TDD([makeQuery(id+"F0.imprint","IMPRINT",EDGE,{"disambiguationData":[TD([[makeQuery(id+"F0.imprint","INTERSECT",VERTEX,{"disambiguationData":[OD(0.0)],"derivedFrom":[sQuery(id+"F0.wireOp",EDGE,"E10"),subQ0]}),-1.0]])],"derivedFrom":subQ0})])],"isStart":false})})])],"isStart":false})});}
            var Q12;
            Q12=makeQuery(id+"F10.boolean.opBoolean","COPY",EDGE,{"derivedFrom":makeQuery(id+"F10.opExtrude","CAP_EDGE",EDGE,{"disambiguationData":[OSD([sQuery(id+"F0.wireOp",EDGE,"E13")])],"isStart":false})});
            var Q13;
            {var subQ0=sQuery(id+"F0.wireOp",EDGE,"E11");Q13=makeQuery(id+"F10.boolean.opBoolean","COPY",EDGE,{"derivedFrom":makeQuery(id+"F10.opExtrude","CAP_EDGE",EDGE,{"disambiguationData":[OSD([subQ0]),TDD([makeQuery(id+"F8.imprint","IMPRINT",EDGE,{"derivedFrom":makeQuery(id+"F1.opExtrude","CAP_EDGE",EDGE,{"disambiguationData":[OSD([subQ0]),TDD([makeQuery(id+"F0.imprint","IMPRINT",EDGE,{"disambiguationData":[TD([[makeQuery(id+"F0.imprint","INTERSECT",VERTEX,{"disambiguationData":[OD(1.0)],"derivedFrom":[sQuery(id+"F0.wireOp",EDGE,"E10"),subQ0]}),1.0]])],"derivedFrom":subQ0})])],"isStart":false})})])],"isStart":false})});}
            chamfer(context, id + "F17", {"entities" : qUnion([Q0, Q1, Q2, Q3, Q4, Q5, Q6, Q7, Q8, Q9, Q10, Q11, Q12, Q13]), "width" : 1 * mm, "tangentPropagation" : true});
        }
        {
            var Q0;
            {var subQ0=sQuery(id+"F0.wireOp",EDGE,"E11");Q0=makeQuery(id+"F11.opExtrude","CAP_EDGE",EDGE,{"disambiguationData":[OSD([subQ0]),TDD([makeQuery(id+"F10.boolean.opBoolean","COPY",EDGE,{"derivedFrom":makeQuery(id+"F10.opExtrude","CAP_EDGE",EDGE,{"disambiguationData":[OSD([subQ0]),TDD([makeQuery(id+"F8.imprint","IMPRINT",EDGE,{"derivedFrom":makeQuery(id+"F1.opExtrude","CAP_EDGE",EDGE,{"disambiguationData":[OSD([subQ0]),TDD([makeQuery(id+"F0.imprint","IMPRINT",EDGE,{"disambiguationData":[TD([[makeQuery(id+"F0.imprint","INTERSECT",VERTEX,{"disambiguationData":[OD(0.0)],"derivedFrom":[sQuery(id+"F0.wireOp",EDGE,"E10"),subQ0]}),-1.0]])],"derivedFrom":subQ0})])],"isStart":false})})])],"isStart":false})})])],"isStart":true});}
            var Q1;
            Q1=makeQuery(id+"F11.opExtrude","CAP_EDGE",EDGE,{"disambiguationData":[OSD([sQuery(id+"F0.wireOp",EDGE,"E10")])],"isStart":true});
            var Q2;
            {var subQ0=sQuery(id+"F0.wireOp",EDGE,"E11");Q2=makeQuery(id+"F11.opExtrude","CAP_EDGE",EDGE,{"disambiguationData":[OSD([subQ0]),TDD([makeQuery(id+"F10.boolean.opBoolean","COPY",EDGE,{"derivedFrom":makeQuery(id+"F10.opExtrude","CAP_EDGE",EDGE,{"disambiguationData":[OSD([subQ0]),TDD([makeQuery(id+"F8.imprint","IMPRINT",EDGE,{"derivedFrom":makeQuery(id+"F1.opExtrude","CAP_EDGE",EDGE,{"disambiguationData":[OSD([subQ0]),TDD([makeQuery(id+"F0.imprint","IMPRINT",EDGE,{"disambiguationData":[TD([[makeQuery(id+"F0.imprint","INTERSECT",VERTEX,{"disambiguationData":[OD(1.0)],"derivedFrom":[sQuery(id+"F0.wireOp",EDGE,"E10"),subQ0]}),1.0]])],"derivedFrom":subQ0})])],"isStart":false})})])],"isStart":false})})])],"isStart":true});}
            var Q3;
            Q3=makeQuery(id+"F11.opExtrude","CAP_EDGE",EDGE,{"disambiguationData":[OSD([sQuery(id+"F0.wireOp",EDGE,"E13")])],"isStart":true});
            chamfer(context, id + "F18", {"entities" : qUnion([Q0, Q1, Q2, Q3]), "width" : 1 * mm, "tangentPropagation" : true});
        }
        {
            var Q0;
            Q0=qCreatedBy(makeId("Right.planeOp"),FACE);
            var sketch = newSketch(context, id + "F19", { "sketchPlane" : qUnion([Q0])});
            skPoint(sketch, "E20", {"position": v(335, -219) * mm});
            skLineSegment(sketch, "E21", {"start": v(335, -219) * mm, "end": v(265, -138.91) * mm});
            skLineSegment(sketch, "E22", {"start": v(265, -138.91) * mm, "end": v(340.91, -138.91) * mm});
            skLineSegment(sketch, "E23", {"start": v(340.91, -138.91) * mm, "end": v(340.91, -218.51) * mm});
            skLineSegment(sketch, "E24", {"start": v(340.91, -218.51) * mm, "end": v(335, -219) * mm});
            skSolve(sketch);
        }
        {
            var Q0;
            Q0=makeQuery(id+"F19.imprint","IMPRINT",FACE,{"disambiguationData":[TD([[makeQuery(id+"F19.imprint","IMPRINT",EDGE,{"derivedFrom":sQuery(id+"F19.wireOp",EDGE,"E21")}),-1.0]])]});
            extrude(context, id + "F20", {"entities" : qUnion([Q0]), "operationType" : NewBodyOperationType.REMOVE, "endBound" : BoundingType.SYMMETRIC, "depth" : 80 * mm, "offsetDistance" : 25 * mm});
        }
    });
